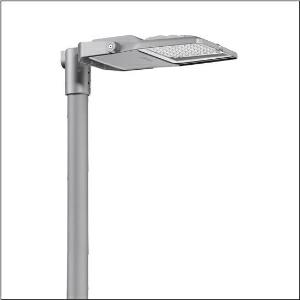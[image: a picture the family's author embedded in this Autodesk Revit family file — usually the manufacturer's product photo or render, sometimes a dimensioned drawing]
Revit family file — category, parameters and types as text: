
# Revit family: floodlight_fl_21_mini___pl43_5xa7775c2a3a_cdc0
name_source: partatom
category: Lighting Fixtures
units: mm (PartAtom-declared; Revit-internal decimal feet)

## family parameters
Cut with Voids When Loaded = No
Host = Face
Light Source = No
Part Type = Normal
Room Calculation Point = No
Round Connector Dimension = Use Diameter
Shared = No

## types (1)
- --- (1 x LED, 12500 lm, 89 W, 3000K)
    Apparent Load = 89 VA
    CIE Flux Codes = 27 78 99 100 100
    Color Rendering = 70
    Color Temperature = 3000K
    Default Elevation = 1800 mm
    Description = Floodlight FL 21 mini, floodlight, primary light control with lens, of PMMA, primary optical cover: protective disc, of toughened safety glass, transparent, light distribution: PL43, light emission: direct distribution, installation type: surface-mounted, LED, High Power LED, rated luminous flux: 12.500lm, luminous efficacy: 140lm/W, light colour: 730, colour temperature: 3000K, control gear: Smart Interface (Zhaga), control: flexible luminous flux parameterisation, time-dependent luminous flux control, constant luminous flux control, overheat protection, pre-setting: logarithmic dimming characteristic, with terminal, 6-pole, mains connection: 220..240V, AC, 50/60Hz, start of lifetime: 89W, end of service life: 94W, reduction: 43W, luminaire housing, of diecast aluminium, powder-coated, SITECO metallic grey (DB 702S), corrosivity category C5 mid according to DIN EN ISO 12944, suitable for swimming pools, chlorine-resistant, sealing non-destructively replaceable, please order mast flange separately, mast bracket, of steel, galvanised, powder-coated, SITECO metallic grey (DB 702S), Smart Interface above, protection rating (complete): IP66, insulation class (complete): insulation class II (safety insulation), certification: CE, ENEC, VDE, protection symbol: D, impact resistance: IK08, permissible operating ambient temperature: -40..+40°C, permissible operating ambient temperature for outdoor applications: -40..+50°C, standard: DIN EN 12944, LABS conformity tested according to VDMA 24364:2018-05, packaging unit: 1 piece

Light Distribution: PL43
    Height = 70 mm
    Lamp = 1 x LED
    Lamp Light Flux = 12500 lm
    Lamp Power = 89 W
    Lamp count = 1
    Length = 485 mm
    Luminous efficacy = 140 lm/W
    Manufacturer = Siteco
    ModVariant = No
    Model = 5XA7775C2A3A
    Mounting Place = Pole
    Mounting Type = Pole annexe
    Number of Poles = 1
    OnlyDefault = Yes
    Power Factor = 1
    Product Name = Floodlight FL 21 mini | PL43
    Product group = floodlight | pylon annexe
    ProductGroupID = 6201
    Protection Class = Protection class II
    Protection Degree = IP 66
    RLX_Detail_Level = 1
    RLX_Emergency_Light_Flux = 0 lm
    RLX_Emergency_Type = 0
    RLX_Emergency_Type_DB = No
    RlxData = <blob elided: 101065 chars, md5=bfbdd400>
    Socket = socket
    Standby Power = 0 W
    System Light Flux = 12500 lm
    System Power = 89 W
    Type Comments = factory setting: luminous flux: 100 % | dim-lin: 254 | 456 mA
    Type Image = l_1007125.jpg
    URL = http://relux.com
    VarID = @adj_162139
    Voltage = 0 V
    Weight = 0.00 kg
    Width = 337 mm

## geometry (parser evidence)
native form markers: Blend x4, Sweep x12
no freeform markers — native parametric forms only
